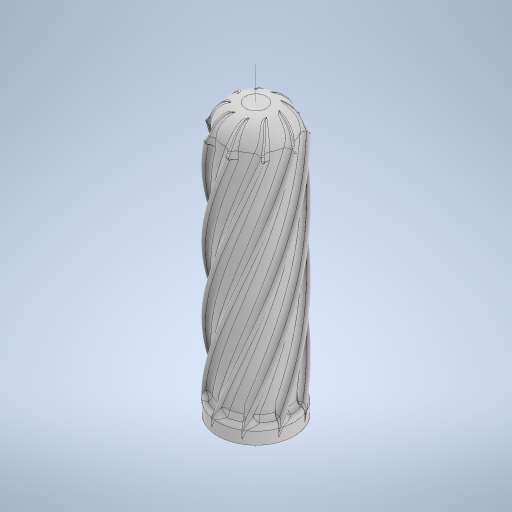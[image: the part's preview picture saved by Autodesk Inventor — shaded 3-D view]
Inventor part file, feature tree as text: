
AUTODESK INVENTOR PART (.ipt)
format: ipt  version: 2023 (Build 270158030, 158C)  size: 1,883,648 bytes
history: native  units: mm
features: fillet x8, sketch x4, projected_geometry x4, extrude x3, helix x1, pattern_circular x1
ambient origin geometry x8: Origin, YZ Plane, XZ Plane, XY Plane, X Axis, Y Axis, Z Axis, Center Point
bodies: Solid1 (feature_tree)
feature tree (21):
  extrude  "Extrusion1"  Depth=49.0mm TaperAngle=0.0deg
  extrude  "Extrusion2"  Depth=7.1mm
  extrude  "Extrusion3"  Depth=3.55mm
  fillet  "Fillet1"  Radius=13.2mm
  helix  "Coil1"  [1 undecoded]
  fillet  "Fillet3"  Radius=46.0mm
  fillet  "Fillet2"  Radius=2.4mm
  fillet  "Fillet7"  Radius=1.2mm
  pattern_circular  "Circular Pattern1"  [2 undecoded]
  fillet  "Fillet8"  Radius=1.0mm
  fillet  "Fillet9"  Radius=90.0mm
  fillet  "Fillet5"  Radius=0.5mm
  fillet  "Fillet6"  Radius=0.5mm
  sketch  "Sketch1"  dims[d0=13.85mm d1=49.0mm d2=0.0mm]
  sketch  "Sketch2"  dims[d3=7.1mm d4=7.1mm]
  sketch  "Sketch3"  dims[d5=3.55mm d6=3.55mm d7=13.2mm d8=0.0mm d9=11.6mm d10=46.0mm d11=0.0mm d12=2.4mm d13=1.2mm]
  projected_geometry  "Projected Loop1"
  sketch  "Sketch4"  dims[d14=70.0mm d15=43.0mm d16=4.0mm d17=0.0mm d18=90.0deg d19=90.0deg d20=0.0mm d21=0.174533mm d22=3.9mm d23=1.0mm d24=1.0mm d26=90.0mm d27=360.0deg d29=0.5mm d30=0.5mm d31=1.0mm d32=1.0mm d33=0.2mm]
  projected_geometry  "Projected Loop2"
  projected_geometry  "Projected Loop3"
  projected_geometry  "Projected Loop4"
note: 3 required parameter values undecoded (feature->parameter linkage not recoverable at this tier; creation-order binding heuristic only, values carry confidence <= 0.55)
